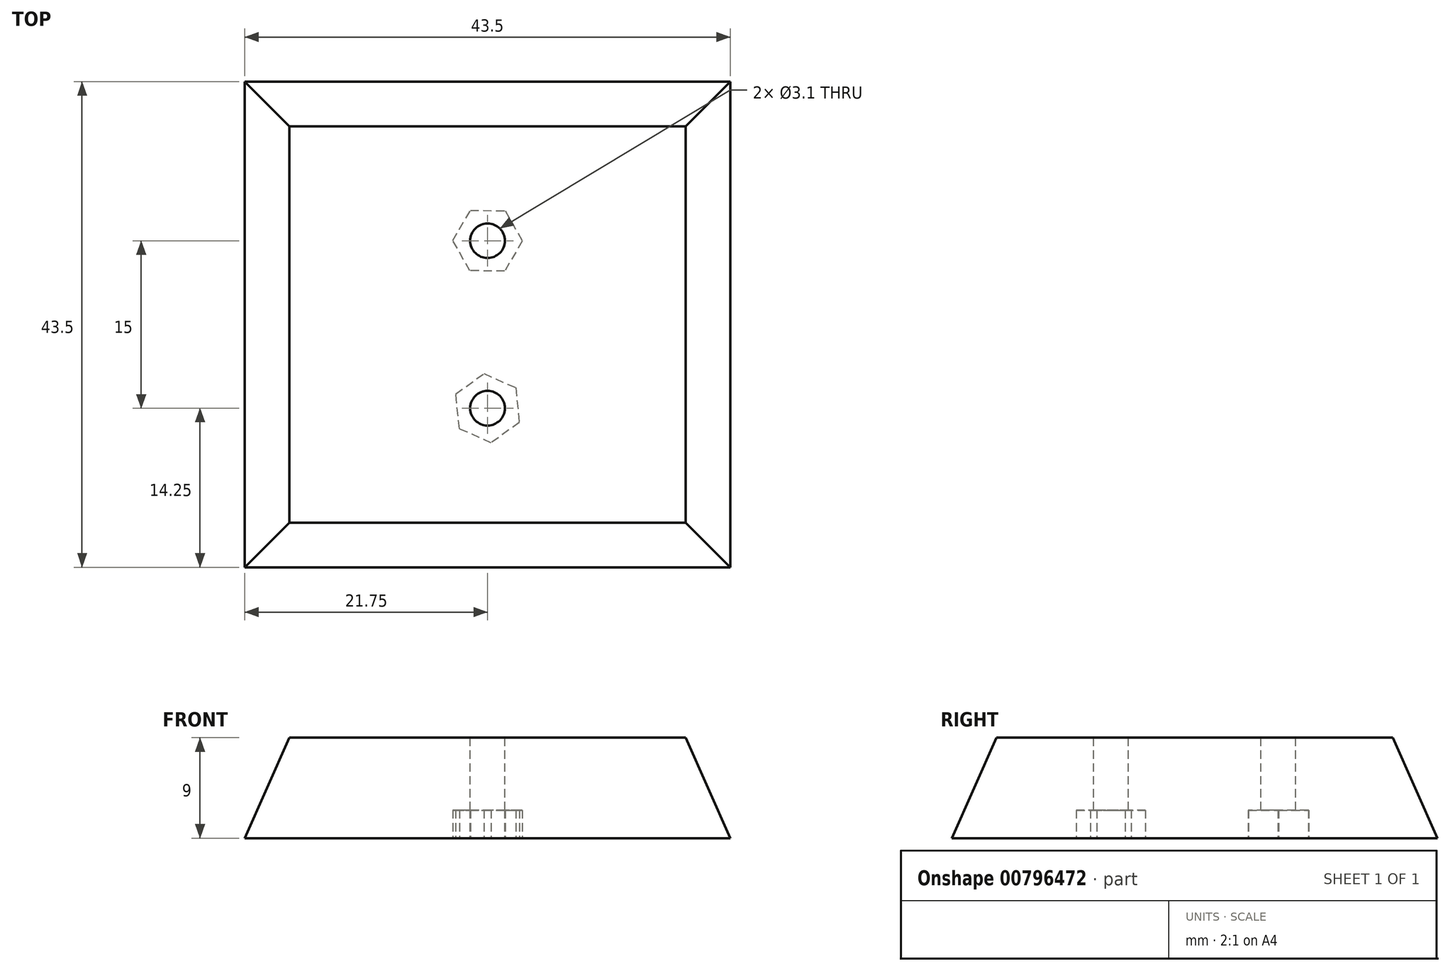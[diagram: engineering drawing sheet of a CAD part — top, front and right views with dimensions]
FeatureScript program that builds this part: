
annotation { "Feature Type Name" : "Feature", "Feature Type Description" : "" }
export const myFeature = defineFeature(function(context is Context, id is Id, definition is map)
    precondition{}
    {
        {
            var Q0;
            Q0=qCreatedBy(makeId("Top.planeOp"),FACE);
            var sketch = newSketch(context, id + "F0", { "sketchPlane" : qUnion([Q0])});
            skLineSegment(sketch, "E0.bottom", {"start": v(21.75, -21.75) * mm, "end": v(-21.75, -21.75) * mm});
            skLineSegment(sketch, "E0.top", {"start": v(21.75, 21.75) * mm, "end": v(-21.75, 21.75) * mm});
            skLineSegment(sketch, "E0.left", {"start": v(21.75, -21.75) * mm, "end": v(21.75, 21.75) * mm});
            skLineSegment(sketch, "E0.right", {"start": v(-21.75, -21.75) * mm, "end": v(-21.75, 21.75) * mm});
            skPoint(sketch, "E0.middle", {"position": v(0, 0) * mm});
            skSolve(sketch);
        }
        {
            assignVariable(context, id + "F1", {"name" : "height", "anyValue" : 9});
        }
        {
            var Q0;
            Q0=makeQuery(id+"F0.imprint","IMPRINT",FACE,{"disambiguationData":[TD([[makeQuery(id+"F0.imprint","IMPRINT",EDGE,{"derivedFrom":sQuery(id+"F0.wireOp",EDGE,"E0.bottom")}),-1.0]])]});
            cPlane(context, id + "F2", {"entities" : qUnion([Q0]), "cplaneType" : CPlaneType.OFFSET, "offset" : (getVariable(context, 'height')) * mm, "width" : 150 * mm, "height" : 150 * mm});
        }
        {
            var Q0;
            Q0=qCreatedBy(id+"F2.planeOp",FACE);
            var sketch = newSketch(context, id + "F3", { "sketchPlane" : qUnion([Q0])});
            skLineSegment(sketch, "E1.bottom", {"start": v(17.75, -17.75) * mm, "end": v(-17.75, -17.75) * mm});
            skLineSegment(sketch, "E1.top", {"start": v(17.75, 17.75) * mm, "end": v(-17.75, 17.75) * mm});
            skLineSegment(sketch, "E1.left", {"start": v(17.75, -17.75) * mm, "end": v(17.75, 17.75) * mm});
            skLineSegment(sketch, "E1.right", {"start": v(-17.75, -17.75) * mm, "end": v(-17.75, 17.75) * mm});
            skPoint(sketch, "E1.middle", {"position": v(0, 0) * mm});
            skSolve(sketch);
        }
        {
            var Q0;
            Q0=makeQuery(id+"F0.imprint","IMPRINT",FACE,{"disambiguationData":[TD([[makeQuery(id+"F0.imprint","IMPRINT",EDGE,{"derivedFrom":sQuery(id+"F0.wireOp",EDGE,"E0.bottom")}),-1.0]])]});
            var Q1;
            Q1=makeQuery(id+"F3.imprint","IMPRINT",FACE,{"disambiguationData":[TD([[makeQuery(id+"F3.imprint","IMPRINT",EDGE,{"derivedFrom":sQuery(id+"F3.wireOp",EDGE,"E1.bottom")}),-1.0]])]});
            loft(context, id + "F4", {"sheetProfilesArray" : [{ "sheetProfileEntities" : qUnion([Q0]) }, { "sheetProfileEntities" : qUnion([Q1]) }]});
        }
        {
            assignVariable(context, id + "F5", {"name" : "nutHeight", "anyValue" : 2.5});
        }
        {
            var Q0;
            Q0=makeQuery(id+"F4.opLoft","CAP_FACE",FACE,{"disambiguationData":[OSD([makeQuery(id+"F3.imprint","IMPRINT",FACE,{"disambiguationData":[TD([[makeQuery(id+"F3.imprint","IMPRINT",EDGE,{"derivedFrom":sQuery(id+"F3.wireOp",EDGE,"E1.bottom")}),-1.0]])]})])],"isStart":true});
            var sketch = newSketch(context, id + "F6", { "sketchPlane" : qUnion([Q0])});
            skLineSegment(sketch, "E2", {"start": v(0, 0) * mm, "end": v(0, -7.5) * mm, "construction": true});
            skLineSegment(sketch, "E3", {"start": v(0, 0) * mm, "end": v(0, 7.5) * mm, "construction": true});
            skCircle(sketch, "E4", {"center": v(0, 7.5) * mm, "radius": 1.55 * mm});
            skCircle(sketch, "E5", {"center": v(0, -7.5) * mm, "radius": 1.55 * mm});
            skSolve(sketch);
        }
        {
            var Q0;
            Q0=qCreatedBy(makeId("Top.planeOp"),FACE);
            var sketch = newSketch(context, id + "F7", { "sketchPlane" : qUnion([Q0])});
            skLineSegment(sketch, "E6", {"start": v(0, 0) * mm, "end": v(0, -7.5) * mm, "construction": true});
            skLineSegment(sketch, "E7", {"start": v(0, 0) * mm, "end": v(0, 7.5) * mm, "construction": true});
            skCircle(sketch, "E8.cCircle", {"center": v(0, -7.5) * mm, "radius": 2.7 * mm, "construction": true});
            skLineSegment(sketch, "E8.0", {"start": v(2.85, -8.77) * mm, "end": v(0.32, -10.6) * mm});
            skLineSegment(sketch, "E8.1", {"start": v(0.32, -10.6) * mm, "end": v(-2.52, -9.33) * mm});
            skLineSegment(sketch, "E8.2", {"start": v(-2.52, -9.33) * mm, "end": v(-2.85, -6.23) * mm});
            skLineSegment(sketch, "E8.3", {"start": v(-2.85, -6.23) * mm, "end": v(-0.32, -4.4) * mm});
            skLineSegment(sketch, "E8.4", {"start": v(-0.32, -4.4) * mm, "end": v(2.52, -5.67) * mm});
            skLineSegment(sketch, "E8.5", {"start": v(2.52, -5.67) * mm, "end": v(2.85, -8.77) * mm});
            skPoint(sketch, "E8.0.midPoint", {"position": v(1.59, -9.69) * mm});
            skCircle(sketch, "E9.cCircle", {"center": v(0, 7.5) * mm, "radius": 2.7 * mm, "construction": true});
            skLineSegment(sketch, "E9.0", {"start": v(1.58, 10.19) * mm, "end": v(3.12, 7.48) * mm});
            skLineSegment(sketch, "E9.1", {"start": v(3.12, 7.48) * mm, "end": v(1.54, 4.79) * mm});
            skLineSegment(sketch, "E9.2", {"start": v(1.54, 4.79) * mm, "end": v(-1.58, 4.81) * mm});
            skLineSegment(sketch, "E9.3", {"start": v(-1.58, 4.81) * mm, "end": v(-3.12, 7.52) * mm});
            skLineSegment(sketch, "E9.4", {"start": v(-3.12, 7.52) * mm, "end": v(-1.54, 10.21) * mm});
            skLineSegment(sketch, "E9.5", {"start": v(-1.54, 10.21) * mm, "end": v(1.58, 10.19) * mm});
            skPoint(sketch, "E9.0.midPoint", {"position": v(2.35, 8.83) * mm});
            skSolve(sketch);
        }
        {
            var Q0;
            Q0=makeQuery(id+"F6.imprint","IMPRINT",FACE,{"disambiguationData":[TD([[makeQuery(id+"F6.imprint","IMPRINT",EDGE,{"derivedFrom":sQuery(id+"F6.wireOp",EDGE,"E4")}),1.0]])]});
            extrude(context, id + "F8", {"entities" : qUnion([Q0]), "operationType" : NewBodyOperationType.REMOVE, "endBound" : BoundingType.THROUGH_ALL, "oppositeDirection" : true, "depth" : 25 * mm, "offsetDistance" : 25 * mm});
        }
        {
            var Q0;
            Q0=makeQuery(id+"F6.imprint","IMPRINT",FACE,{"disambiguationData":[TD([[makeQuery(id+"F6.imprint","IMPRINT",EDGE,{"derivedFrom":sQuery(id+"F6.wireOp",EDGE,"E5")}),1.0]])]});
            extrude(context, id + "F9", {"entities" : qUnion([Q0]), "operationType" : NewBodyOperationType.REMOVE, "endBound" : BoundingType.THROUGH_ALL, "oppositeDirection" : true, "depth" : 25 * mm, "offsetDistance" : 25 * mm});
        }
        {
            var Q0;
            Q0=makeQuery(id+"F7.imprint","IMPRINT",FACE,{"disambiguationData":[TD([[makeQuery(id+"F7.imprint","IMPRINT",EDGE,{"derivedFrom":sQuery(id+"F7.wireOp",EDGE,"E8.0")}),-1.0]])]});
            extrude(context, id + "F10", {"entities" : qUnion([Q0]), "operationType" : NewBodyOperationType.REMOVE, "depth" : (getVariable(context, 'nutHeight')) * mm, "offsetDistance" : 25 * mm});
        }
        {
            var Q0;
            Q0=makeQuery(id+"F7.imprint","IMPRINT",FACE,{"disambiguationData":[TD([[makeQuery(id+"F7.imprint","IMPRINT",EDGE,{"derivedFrom":sQuery(id+"F7.wireOp",EDGE,"E9.0")}),-1.0]])]});
            extrude(context, id + "F11", {"entities" : qUnion([Q0]), "operationType" : NewBodyOperationType.REMOVE, "depth" : (getVariable(context, 'nutHeight')) * mm, "offsetDistance" : 25 * mm});
        }
    });
